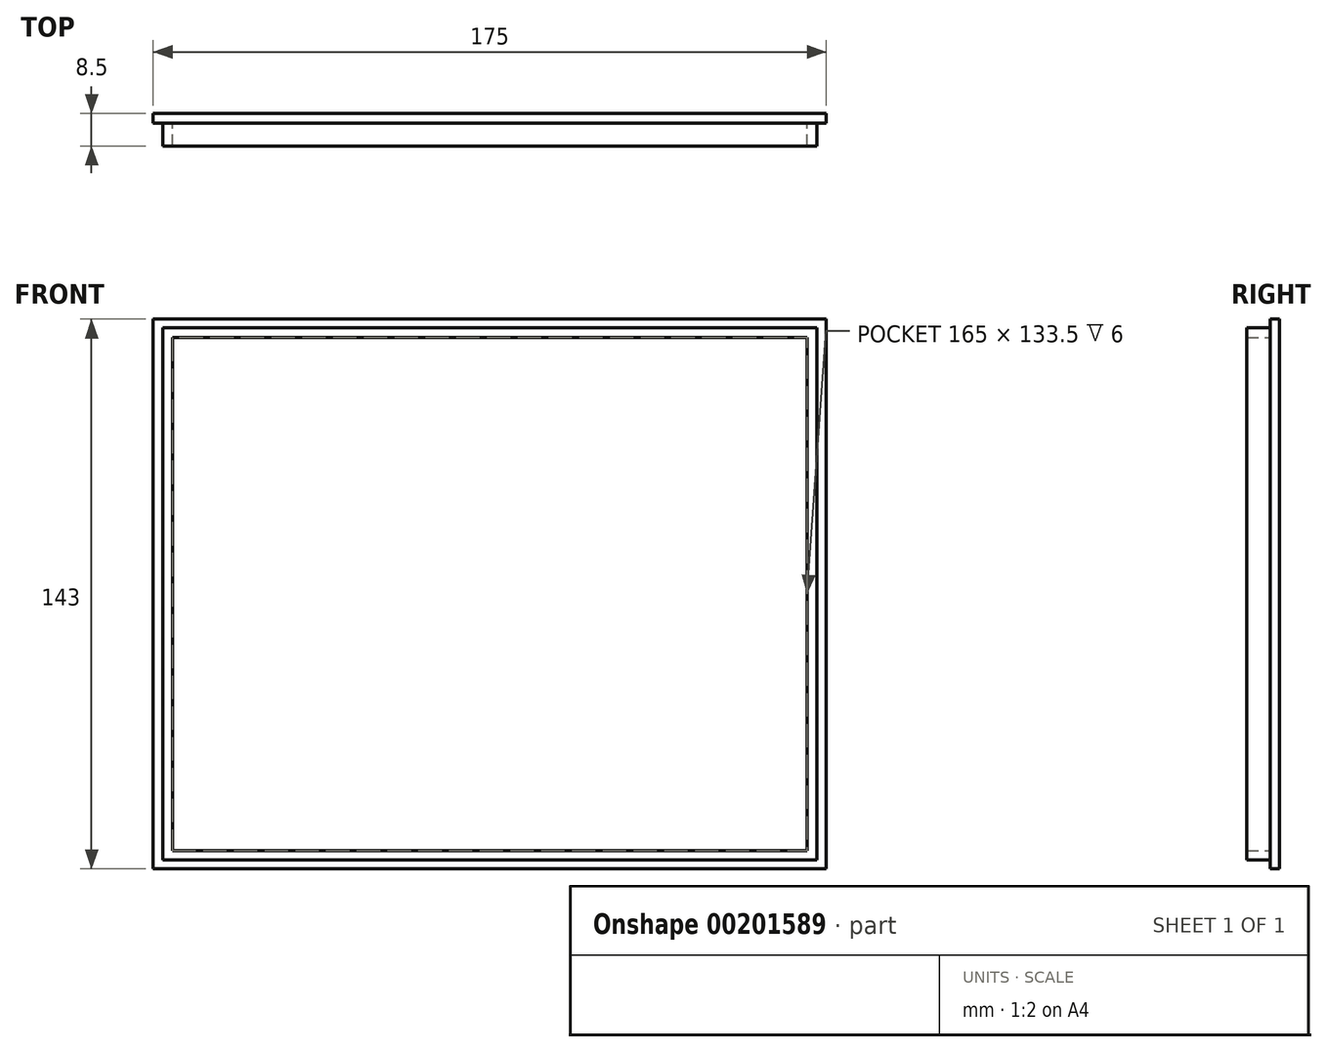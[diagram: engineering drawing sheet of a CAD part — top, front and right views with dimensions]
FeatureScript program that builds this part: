
annotation { "Feature Type Name" : "Feature", "Feature Type Description" : "" }
export const myFeature = defineFeature(function(context is Context, id is Id, definition is map)
    precondition{}
    {
        {
            var Q0;
            Q0=qCreatedBy(makeId("Front.planeOp"),FACE);
            var sketch = newSketch(context, id + "F0", { "sketchPlane" : qUnion([Q0])});
            skLineSegment(sketch, "E0.bottom", {"start": v(87.5, -71.5) * mm, "end": v(-87.5, -71.5) * mm});
            skLineSegment(sketch, "E0.top", {"start": v(87.5, 71.5) * mm, "end": v(-87.5, 71.5) * mm});
            skLineSegment(sketch, "E0.left", {"start": v(87.5, -71.5) * mm, "end": v(87.5, 71.5) * mm});
            skLineSegment(sketch, "E0.right", {"start": v(-87.5, -71.5) * mm, "end": v(-87.5, 71.5) * mm});
            skPoint(sketch, "E0.middle", {"position": v(0, 0) * mm});
            skSolve(sketch);
        }
        {
            var Q0;
            Q0 = qSketchRegion(id + "F0", true);
            extrude(context, id + "F1", {"entities" : qUnion([Q0]), "depth" : 2.5 * mm});
        }
        {
            var Q0;
            Q0=makeQuery(id+"F1.opExtrude","CAP_FACE",FACE,{"disambiguationData":[OSD([sQuery(id+"F0.wireOp",EDGE,"E0.bottom"),sQuery(id+"F0.wireOp",EDGE,"E0.top"),sQuery(id+"F0.wireOp",EDGE,"E0.left"),sQuery(id+"F0.wireOp",EDGE,"E0.right")])],"isStart":false});
            var sketch = newSketch(context, id + "F2", { "sketchPlane" : qUnion([Q0])});
            skLineSegment(sketch, "E1.bottom", {"start": v(85, -69.25) * mm, "end": v(-85, -69.25) * mm});
            skLineSegment(sketch, "E1.top", {"start": v(85, 69.25) * mm, "end": v(-85, 69.25) * mm});
            skLineSegment(sketch, "E1.left", {"start": v(85, -69.25) * mm, "end": v(85, 69.25) * mm});
            skLineSegment(sketch, "E1.right", {"start": v(-85, -69.25) * mm, "end": v(-85, 69.25) * mm});
            skPoint(sketch, "E1.middle", {"position": v(0, 0) * mm});
            skSolve(sketch);
        }
        {
            var Q0;
            Q0 = qSketchRegion(id + "F2", true);
            extrude(context, id + "F3", {"entities" : qUnion([Q0]), "operationType" : NewBodyOperationType.ADD, "depth" : 6 * mm});
        }
        {
            var Q0;
            Q0=makeQuery(id+"F3.opExtrude","CAP_FACE",FACE,{"disambiguationData":[OSD([sQuery(id+"F2.wireOp",EDGE,"E1.bottom"),sQuery(id+"F2.wireOp",EDGE,"E1.top"),sQuery(id+"F2.wireOp",EDGE,"E1.left"),sQuery(id+"F2.wireOp",EDGE,"E1.right")])],"isStart":false});
            shell(context, id + "F4", {"entities" : qUnion([Q0]), "thickness" : 2.5 * mm});
        }
    });
